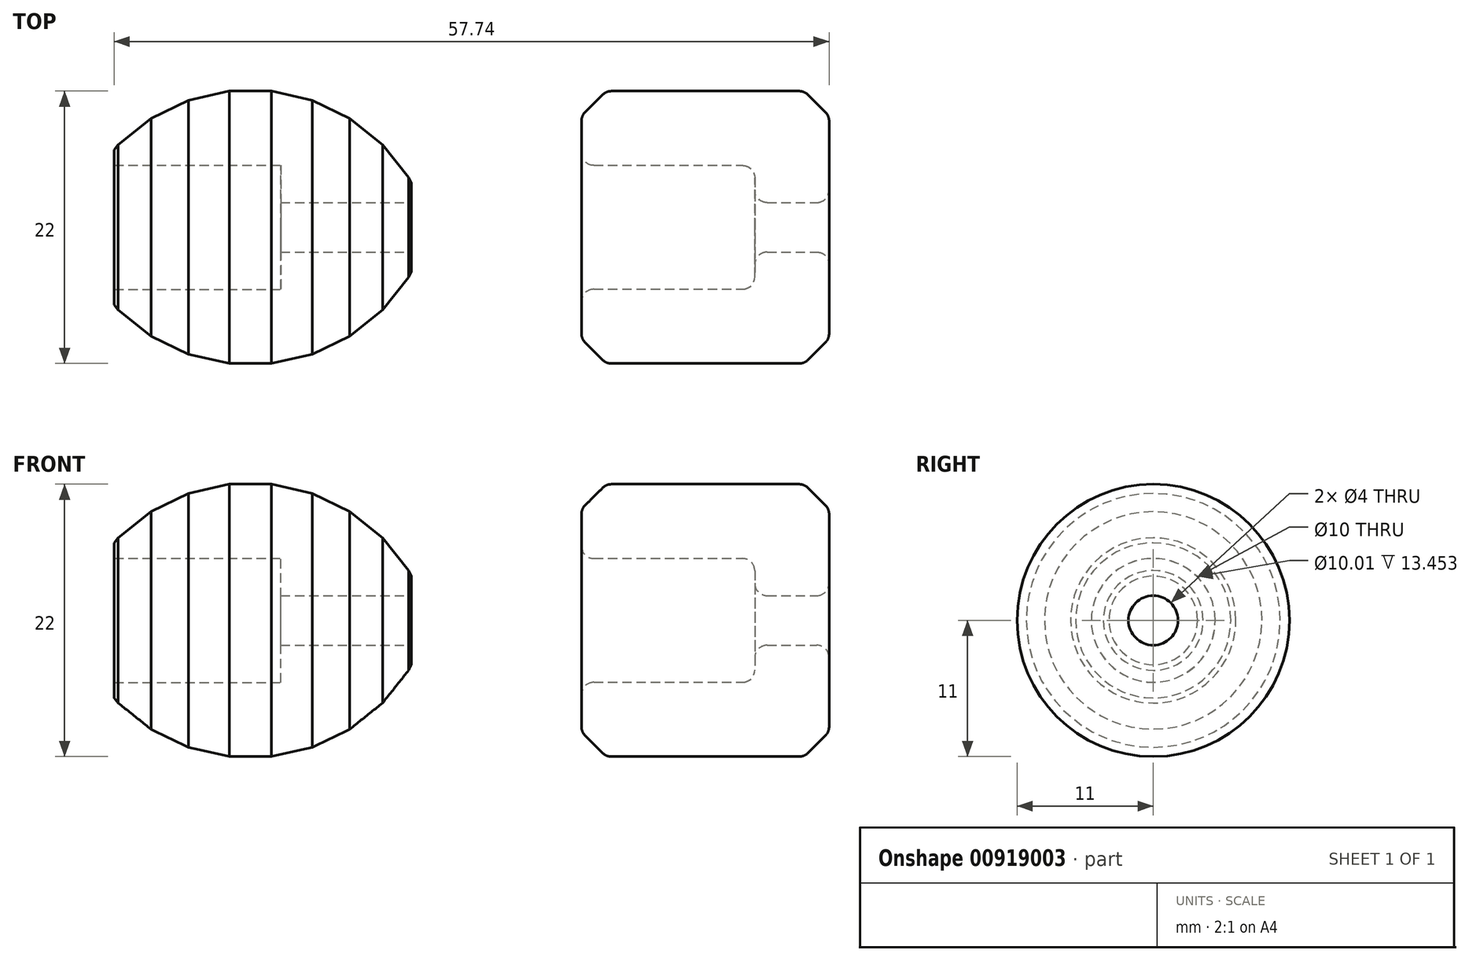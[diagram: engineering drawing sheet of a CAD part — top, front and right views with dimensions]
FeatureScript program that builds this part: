
annotation { "Feature Type Name" : "Feature", "Feature Type Description" : "" }
export const myFeature = defineFeature(function(context is Context, id is Id, definition is map)
    precondition{}
    {
        {
            var Q0;
            Q0=qCreatedBy(makeId("Front.planeOp"),FACE);
            var sketch = newSketch(context, id + "F0", { "sketchPlane" : qUnion([Q0])});
            skLineSegment(sketch, "E0", {"start": v(0, 0) * mm, "end": v(0, 2) * mm});
            skLineSegment(sketch, "E1", {"start": v(0, 0) * mm, "end": v(-5, 0) * mm});
            skLineSegment(sketch, "E2", {"start": v(0, 0) * mm, "end": v(0, 11) * mm});
            skLineSegment(sketch, "E3", {"start": v(0, 11) * mm, "end": v(-24, 11) * mm});
            skLineSegment(sketch, "E4", {"start": v(-24, 11) * mm, "end": v(-24, 5) * mm});
            skPoint(sketch, "E5.endSnap0", {"position": v(-12, 11) * mm});
            skLineSegment(sketch, "E6", {"start": v(-12, 11) * mm, "end": v(-12, -4) * mm});
            skLineSegment(sketch, "E7", {"start": v(-24, 5) * mm, "end": v(-10.55, 5) * mm});
            skLineSegment(sketch, "E8", {"start": v(-10.55, 5) * mm, "end": v(-10.55, 2) * mm});
            skLineSegment(sketch, "E9", {"start": v(-10.55, 2) * mm, "end": v(0, 2) * mm});
            skLineSegment(sketch, "E10", {"start": v(-12, 11) * mm, "end": v(-13, 11) * mm});
            skLineSegment(sketch, "E11", {"start": v(-13, 11) * mm, "end": v(-13, -4) * mm});
            skLineSegment(sketch, "E12.0", {"start": v(-14.7, 11) * mm, "end": v(-11.3, 11) * mm});
            skLineSegment(sketch, "E12.1", {"start": v(-11.3, 11) * mm, "end": v(-8.01, 10.25) * mm});
            skLineSegment(sketch, "E12.2", {"start": v(-8.01, 10.25) * mm, "end": v(-4.97, 8.78) * mm});
            skLineSegment(sketch, "E12.3", {"start": v(-4.97, 8.78) * mm, "end": v(-2.33, 6.67) * mm});
            skLineSegment(sketch, "E12.4", {"start": v(-2.33, 6.67) * mm, "end": v(-0.22, 4.03) * mm});
            skLineSegment(sketch, "E12.5", {"start": v(-0.22, 4.03) * mm, "end": v(0, 3.58) * mm});
            skLineSegment(sketch, "E12.24", {"start": v(-24, 6.26) * mm, "end": v(-23.67, 6.67) * mm});
            skLineSegment(sketch, "E12.25", {"start": v(-23.67, 6.67) * mm, "end": v(-21.03, 8.78) * mm});
            skLineSegment(sketch, "E12.26", {"start": v(-21.03, 8.78) * mm, "end": v(-17.99, 10.25) * mm});
            skLineSegment(sketch, "E12.27", {"start": v(-17.99, 10.25) * mm, "end": v(-14.7, 11) * mm});
            skPoint(sketch, "E12.0.midPoint", {"position": v(-13, 11) * mm});
            skArc(sketch, "E13.trimOffspring", {"start": v(0, 3.48) * mm, "mid": v(-11.31, 10.9) * mm, "end": v(-24, 6.2) * mm, "construction": true});
            skSolve(sketch);
        }
        {
            var Q0;
            {var subQ7=sQuery(id+"F0.wireOp",EDGE,"E8");Q0=makeQuery(id+"F0.imprint","IMPRINT",FACE,{"disambiguationData":[TD([[makeQuery(id+"F0.imprint","IMPRINT",EDGE,{"derivedFrom":subQ7}),1.0]])]});}
            var Q1;
            {var subQ0=sQuery(id+"F0.wireOp",EDGE,"E12.0");var subQ1=sQuery(id+"F0.wireOp",EDGE,"E6");var subQ2=makeQuery(id+"F0.imprint","INTERSECT",VERTEX,{"derivedFrom":[subQ1,subQ0]});Q1=makeQuery(id+"F0.imprint","IMPRINT",FACE,{"disambiguationData":[TD([[makeQuery(id+"F0.imprint","IMPRINT",EDGE,{"disambiguationData":[TD([[subQ2,-1.0]])],"derivedFrom":subQ1}),-1.0]])]});}
            var Q2;
            {var subQ8=sQuery(id+"F0.wireOp",EDGE,"E12.24");Q2=makeQuery(id+"F0.imprint","IMPRINT",FACE,{"disambiguationData":[TD([[makeQuery(id+"F0.imprint","IMPRINT",EDGE,{"derivedFrom":subQ8}),-1.0]])]});}
            var Q3;
            Q3=sQuery(id+"F0.wireOp",EDGE,"E1");
            revolve(context, id + "F1", {"surfaceOperationType" : NewSurfaceOperationType.NEW, "entities" : qUnion([Q0, Q1, Q2]), "axis" : qUnion([Q3]), "revolveType" : RevolveType.FULL});
        }
        {
            var Q0;
            Q0=qCreatedBy(makeId("Front.planeOp"),FACE);
            var sketch = newSketch(context, id + "F2", { "sketchPlane" : qUnion([Q0])});
            skLineSegment(sketch, "E14", {"start": v(33.74, 0) * mm, "end": v(33.74, 2) * mm});
            skLineSegment(sketch, "E15", {"start": v(33.74, 0) * mm, "end": v(28.74, 0) * mm});
            skLineSegment(sketch, "E16", {"start": v(33.74, 0) * mm, "end": v(33.74, 11) * mm});
            skLineSegment(sketch, "E17", {"start": v(33.74, 11) * mm, "end": v(13.74, 11) * mm});
            skLineSegment(sketch, "E18", {"start": v(13.74, 11) * mm, "end": v(13.74, 5) * mm});
            skLineSegment(sketch, "E19", {"start": v(13.74, 5) * mm, "end": v(27.74, 5) * mm});
            skLineSegment(sketch, "E20", {"start": v(27.74, 5) * mm, "end": v(27.74, 2) * mm});
            skLineSegment(sketch, "E21", {"start": v(27.74, 2) * mm, "end": v(33.74, 2) * mm});
            skSolve(sketch);
        }
        {
            var Q0;
            Q0 = qSketchRegion(id + "F2", true);
            var Q1;
            Q1=sQuery(id+"F2.wireOp",EDGE,"E15");
            revolve(context, id + "F3", {"surfaceOperationType" : NewSurfaceOperationType.NEW, "entities" : qUnion([Q0]), "axis" : qUnion([Q1]), "revolveType" : RevolveType.FULL});
        }
        {
            var Q0;
            Q0=makeQuery(id+"F3.opRevolve","SWEPT_FACE",FACE,{"disambiguationData":[OSD([sQuery(id+"F2.wireOp",EDGE,"E17")])]});
            chamfer(context, id + "F4", {"entities" : qUnion([Q0]), "width" : 2 * mm, "tangentPropagation" : true});
        }
        {
            var Q0;
            Q0=makeQuery(id+"F3.opRevolve","SWEPT_FACE",FACE,{"disambiguationData":[OSD([sQuery(id+"F2.wireOp",EDGE,"E19")])]});
            var Q1;
            Q1=makeQuery(id+"F3.opRevolve","SWEPT_FACE",FACE,{"disambiguationData":[OSD([sQuery(id+"F2.wireOp",EDGE,"E21")])]});
            fillet(context, id + "F5", {"entities" : qUnion([Q0, Q1]), "radius" : 1 * mm, "tangentPropagation" : true, "allowEdgeOverflow" : false});
        }
        {
            var Q0;
            Q0=makeQuery(id+"F3.opRevolve","SWEPT_FACE",FACE,{"disambiguationData":[OSD([sQuery(id+"F2.wireOp",EDGE,"E17")])]});
            var Q1;
            Q1=makeQuery(id+"F4.opChamfer","BLEND_FACE",FACE,{"disambiguationData":[OSD([sQuery(id+"F2.wireOp",EDGE,"E16"),sQuery(id+"F2.wireOp",EDGE,"E17")])]});
            var Q2;
            Q2=makeQuery(id+"F4.opChamfer","BLEND_FACE",FACE,{"disambiguationData":[OSD([sQuery(id+"F2.wireOp",EDGE,"E17"),sQuery(id+"F2.wireOp",EDGE,"E18")])]});
            fillet(context, id + "F6", {"entities" : qUnion([Q0, Q1, Q2]), "radius" : 1 * mm, "tangentPropagation" : true, "allowEdgeOverflow" : false});
        }
    });
